# Revit family: BIG MAX_L
name_source: partatom
category: Plumbing Fixtures
units: mm (PartAtom-declared; Revit-internal decimal feet)

## family parameters
Always vertical = Yes
Cut with Voids When Loaded = Yes
OmniClass Number = 23.45.00.00
OmniClass Title = Sanitary, Laundry, and Cleaning Equipment
Part Type = Normal
Room Calculation Point = No
Round Connector Dimension = Use Diameter
Shared = No
Work Plane-Based = No

## types (3) — shared parameters
Manufacturer = MIFAB
Material = Polyethylene, High Density
array = 2

## per-type parameters (varying)
| type | Description | Ext End | Front Extude | Height of Body | Length | Lid Height from Inlet/Outlet Center (15.5" Min. thru 24.5" Max.) | Model | Pipe RP | Top RP 1 | URL | Visibility-1 | Visiblity | Void 1 H | Void 1 L | Void 1 TL | Width | center void | center void h | pipe height | v1 | v2 |
| BIG-300-L | 300 gal/ft3 Big Max HDPE Lint Interceptor | -20" | 27 1/2" | 50" | 83" | 24 1/4" | XL-MI-G-PL-300 | 38" | 19" | www,mifab.com | No | Yes | 7" | 14" | 12" | 33 1/2" | 10" | 4 1/4" | 12 1/2" | No | Yes |
| BIG-140-L | 140 gal/ft3 Big Max HDPE Lint Interceptor | -16" | 20 3/4" | 37" | 50" | 24 1/4" | XL-MI-G-PL-140 | 25 1/2" | 14" | www.mifab.com | No | Yes | 4" | 7" | 8" | 33 1/2" | 2" | 2" | 12 3/4" | Yes | No |
| BIG-55-L | 55 gal/ft3 Big Max HDPE Lint Interceptor
gallons. | -12" | 13 1/2" | 26" | 37" | 24 1/2" | XL-MI-G-PL-55 | 13 1/2" | 9" | www.mifab.com | Yes | No | 3" | 3" | 6" | 28" | 2" | 2" | 12 3/4" | No | No |

## geometry (parser evidence)
native form markers: Sweep x8
no freeform markers — native parametric forms only
